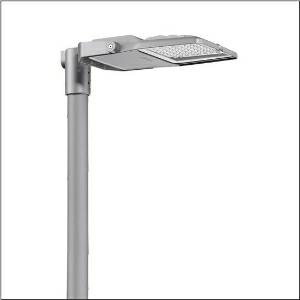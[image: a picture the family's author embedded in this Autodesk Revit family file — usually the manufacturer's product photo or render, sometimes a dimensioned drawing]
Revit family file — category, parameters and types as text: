
# Revit family: floodlight_fl_21_mini___pl52_5xa7776c2d3a_1d2c
name_source: partatom
category: Lighting Fixtures
units: mm (PartAtom-declared; Revit-internal decimal feet)

## family parameters
Cut with Voids When Loaded = No
Host = Face
Light Source = No
Part Type = Normal
Room Calculation Point = No
Round Connector Dimension = Use Diameter
Shared = No

## types (1)
- --- (1 x LED, 12190 lm, 89 W, 3000K)
    Apparent Load = 89 VA
    CIE Flux Codes = 26 60 98 100 100
    Color Rendering = 70
    Color Temperature = 3000K
    Default Elevation = 1800 mm
    Description = Floodlight FL 21 mini, floodlight, primary light control with lens, of PMMA, primary optical cover: protective disc, of toughened safety glass, transparent, light distribution: PL52, light emission: direct distribution, installation type: surface-mounted, LED, High Power LED, rated luminous flux: 12.190lm, luminous efficacy: 137lm/W, light colour: 730, colour temperature: 3000K, control gear: Smart Interface (Zhaga), control: flexible luminous flux parameterisation, time-dependent luminous flux control, constant luminous flux control, overheat protection, pre-setting: logarithmic dimming characteristic, with terminal, 6-pole, mains connection: 220..240V, AC, 50/60Hz, start of lifetime: 89W, end of service life: 94W, reduction: 43W, luminaire housing, of diecast aluminium, powder-coated, Siteco® metallic grey (DB 702S), corrosivity category C5 mid according to DIN EN ISO 12944, suitable for swimming pools, chlorine-resistant, sealing non-destructively replaceable, please order mast flange separately, mast bracket, of steel, galvanised, powder-coated, Siteco® metallic grey (DB 702S), Smart Interface below and above, protection rating (complete): IP66, insulation class (complete): insulation class II (safety insulation), certification: CE, ENEC, VDE, protection symbol: D, impact resistance: IK08, permissible operating ambient temperature: -40..+40°C, permissible operating ambient temperature for outdoor applications: -40..+50°C, standard: DIN EN 12944, LABS conformity tested according to VDMA 24364:2018-05, packaging unit: 1 piece

Light Distribution: PL52
    Height = 70 mm
    Lamp = 1 x LED
    Lamp Light Flux = 12190 lm
    Lamp Power = 89 W
    Lamp count = 1
    Length = 485 mm
    Luminous efficacy = 137 lm/W
    Manufacturer = Siteco
    ModVariant = No
    Model = 5XA7776C2D3A
    Number of Poles = 1
    OnlyDefault = Yes
    Power Factor = 1
    Product Name = Floodlight FL 21 mini | PL52
    Product group = floodlight | pylon annexe
    ProductGroupID = 6200
    Protection Class = Protection class II
    Protection Degree = IP 66
    RLX_Detail_Level = 1
    RLX_Emergency_Light_Flux = 0 lm
    RLX_Emergency_Type = 0
    RLX_Emergency_Type_DB = No
    RlxData = <blob elided: 101101 chars, md5=ad8a81da>
    Socket = socket
    Standby Power = 0 W
    System Light Flux = 12190 lm
    System Power = 89 W
    Type Comments = factory setting: luminous flux: 100 % | dim-lin: 254 | 456 mA
    Type Image = l_1007125.jpg
    URL = http://relux.com
    VarID = @adj_163258
    Voltage = 0 V
    Weight = 0.00 kg
    Width = 337 mm

## geometry (parser evidence)
native form markers: Blend x4, Sweep x13
no freeform markers — native parametric forms only
